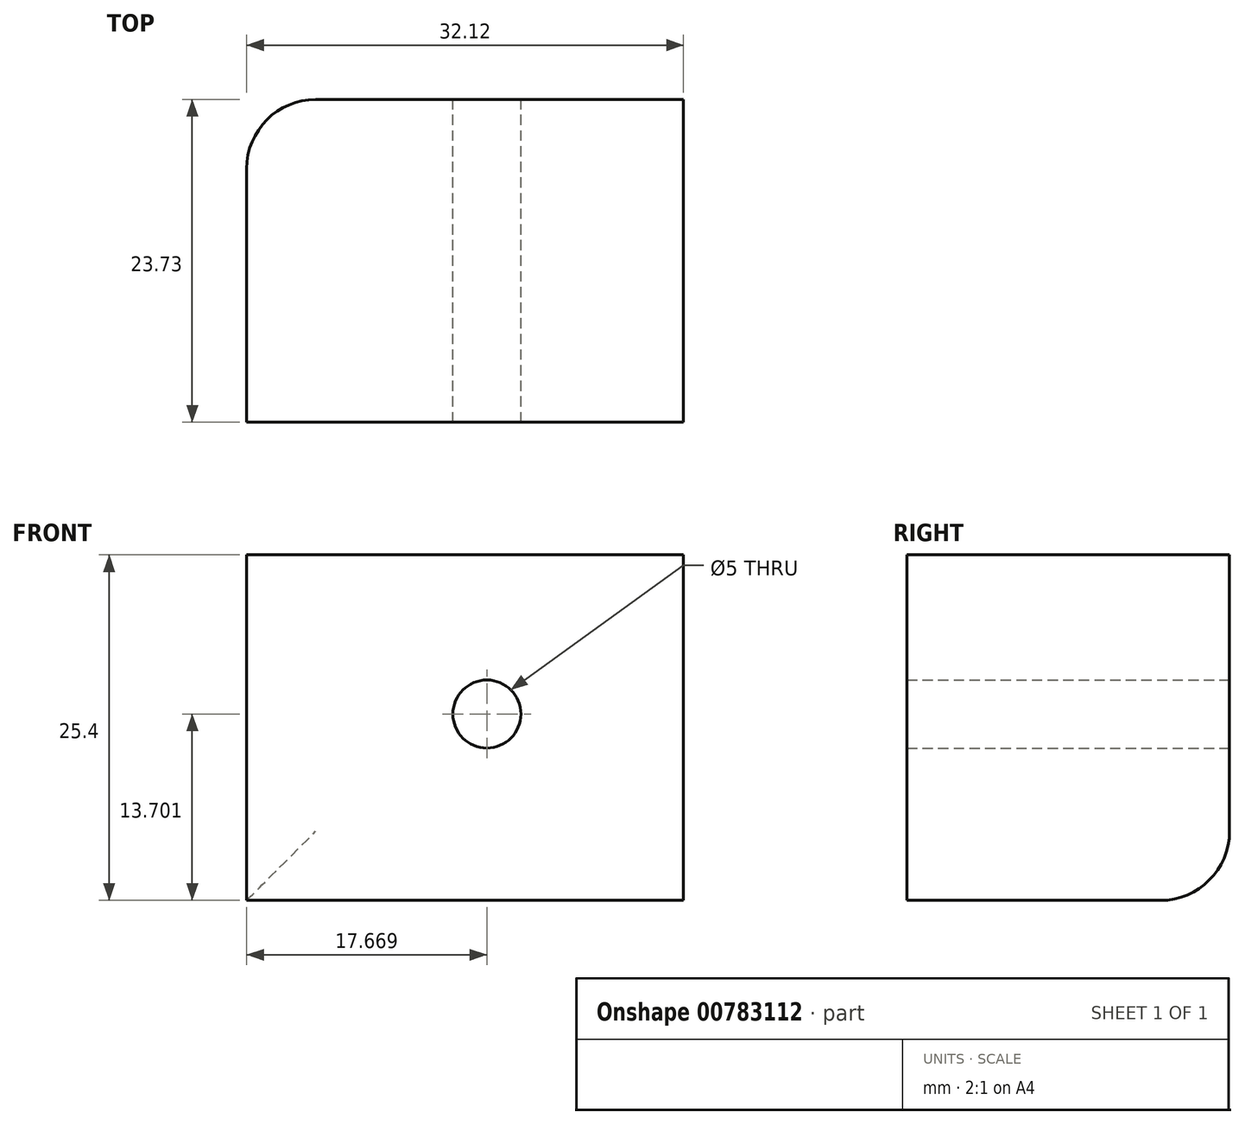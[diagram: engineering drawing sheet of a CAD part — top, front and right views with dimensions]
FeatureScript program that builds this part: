
annotation { "Feature Type Name" : "Feature", "Feature Type Description" : "" }
export const myFeature = defineFeature(function(context is Context, id is Id, definition is map)
    precondition{}
    {
        {
            var Q0;
            Q0=qCreatedBy(makeId("Top.planeOp"),FACE);
            var sketch = newSketch(context, id + "F0", { "sketchPlane" : qUnion([Q0])});
            skLineSegment(sketch, "E0", {"start": v(0, 0) * mm, "end": v(0, 23.73) * mm});
            skLineSegment(sketch, "E1", {"start": v(0, 23.73) * mm, "end": v(32.12, 23.73) * mm});
            skLineSegment(sketch, "E2", {"start": v(32.12, 23.73) * mm, "end": v(32.12, 0) * mm});
            skLineSegment(sketch, "E3", {"start": v(32.12, 0) * mm, "end": v(0, 0) * mm});
            skSolve(sketch);
        }
        {
            var Q0;
            Q0=makeQuery(id+"F0.imprint","IMPRINT",FACE,{"disambiguationData":[TD([[makeQuery(id+"F0.imprint","IMPRINT",EDGE,{"derivedFrom":sQuery(id+"F0.wireOp",EDGE,"E0")}),-1.0]])]});
            extrude(context, id + "F1", {"entities" : qUnion([Q0]), "depth" : 25.4 * mm, "offsetDistance" : 25.4 * mm});
        }
        {
            var Q0;
            Q0=makeQuery(id+"F1.opExtrude","SWEPT_EDGE",EDGE,{"disambiguationData":[OSD([sQuery(id+"F0.wireOp",EDGE,"E0"),sQuery(id+"F0.wireOp",EDGE,"E1")])]});
            var Q1;
            Q1=makeQuery(id+"F1.opExtrude","CAP_EDGE",EDGE,{"disambiguationData":[OSD([sQuery(id+"F0.wireOp",EDGE,"E1")])],"isStart":true});
            fillet(context, id + "F2", {"entities" : qUnion([Q0, Q1]), "radius" : 5.08 * mm, "tangentPropagation" : true, "allowEdgeOverflow" : false});
        }
        {
            var Q0;
            Q0=makeQuery(id+"F1.opExtrude","SWEPT_FACE",FACE,{"disambiguationData":[OSD([sQuery(id+"F0.wireOp",EDGE,"E1")])]});
            var sketch = newSketch(context, id + "F3", { "sketchPlane" : qUnion([Q0])});
            skPoint(sketch, "E4", {"position": v(-17.67, 13.7) * mm});
            skSolve(sketch);
        }
        {
            var Q0;
            Q0=sQuery(id+"F3.wireOp",VERTEX,"E4");
            var Q1;
            Q1=makeQuery(id+"F1.opExtrude","SWEPT_BODY",BODY,{"disambiguationData":[OSD([sQuery(id+"F0.wireOp",EDGE,"E0"),sQuery(id+"F0.wireOp",EDGE,"E1"),sQuery(id+"F0.wireOp",EDGE,"E2"),sQuery(id+"F0.wireOp",EDGE,"E3")])]});
            hole(context, id + "F4", {"style" : HoleStyle.SIMPLE, "endStyle" : HoleEndStyle.THROUGH, "standardTappedOrClearance" : lookupTablePath({ "standard" : "ISO", "size" : "5", "type" : "Drilled" }), "standardBlindInLast" : lookupTablePath({ "standard" : "ISO", "size" : "5", "type" : "Drilled" }), "holeDiameter" : 5 * mm, "majorDiameter" : 6.35 * mm, "isTappedThrough" : true, "tappedDepth" : 12.7 * mm, "tapClearance" : 3, "locations" : qUnion([Q0]), "scope" : qUnion([Q1])});
        }
    });
